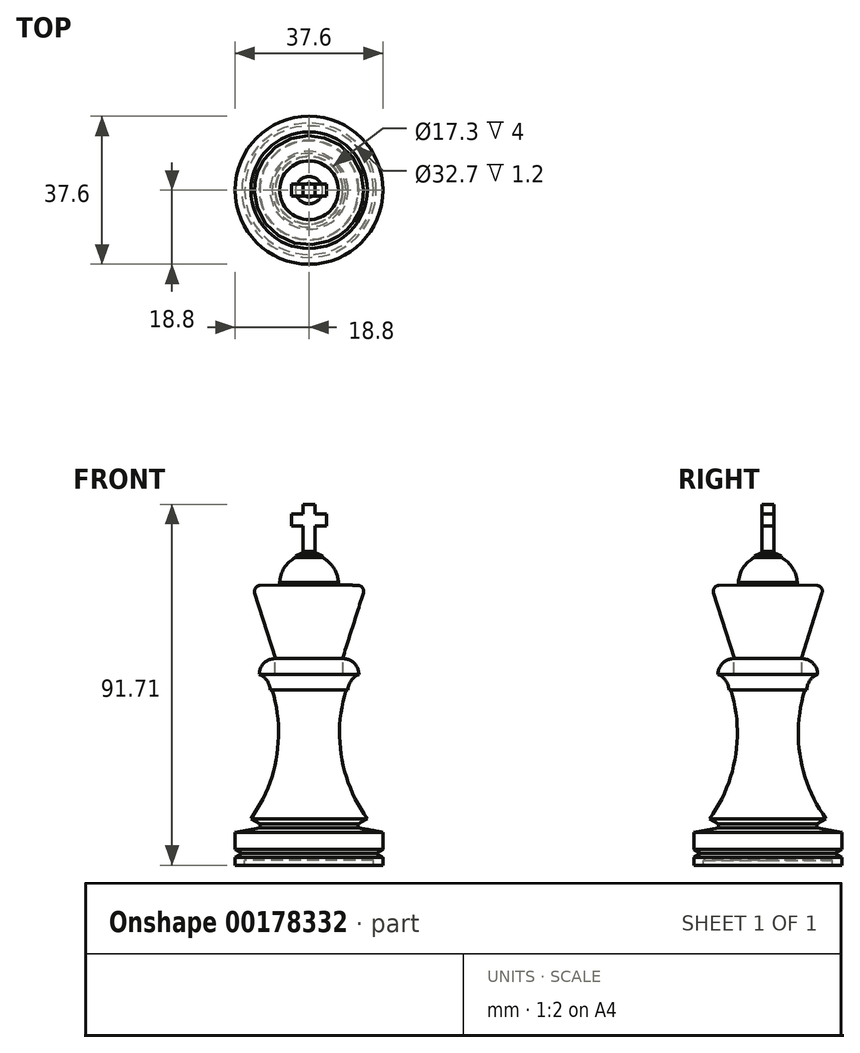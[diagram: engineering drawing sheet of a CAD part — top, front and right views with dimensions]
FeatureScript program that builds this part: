
annotation { "Feature Type Name" : "Feature", "Feature Type Description" : "" }
export const myFeature = defineFeature(function(context is Context, id is Id, definition is map)
    precondition{}
    {
        {
            var Q0;
            Q0=qCreatedBy(makeId("Front.planeOp"),FACE);
            var sketch = newSketch(context, id + "F0", { "sketchPlane" : qUnion([Q0])});
            skLineSegment(sketch, "E0", {"start": v(18.8, 2) * mm, "end": v(17.07, 3) * mm});
            skLineSegment(sketch, "E1", {"start": v(18.8, 0) * mm, "end": v(16.35, 0) * mm});
            skLineSegment(sketch, "E2", {"start": v(18.8, 0) * mm, "end": v(18.8, 2) * mm});
            skLineSegment(sketch, "E3", {"start": v(0, 79) * mm, "end": v(0, 0) * mm});
            skLineSegment(sketch, "E4", {"start": v(12.5, 9.5) * mm, "end": v(12.5, 10.5) * mm});
            skLineSegment(sketch, "E5", {"start": v(35.59, 2) * mm, "end": v(35.59, 3) * mm});
            skLineSegment(sketch, "E6", {"start": v(18.8, 4) * mm, "end": v(17.07, 3) * mm});
            skLineSegment(sketch, "E7", {"start": v(12.5, 9.5) * mm, "end": v(18.8, 8.36) * mm});
            skLineSegment(sketch, "E8", {"start": v(18.8, 4) * mm, "end": v(18.8, 8.36) * mm});
            skLineSegment(sketch, "E9", {"start": v(16.35, 1.2) * mm, "end": v(16.35, 0) * mm});
            skLineSegment(sketch, "E10", {"start": v(0, 1.2) * mm, "end": v(16.35, 1.2) * mm});
            skLineSegment(sketch, "E11", {"start": v(12.5, 10.5) * mm, "end": v(14.8, 11.83) * mm});
            skPoint(sketch, "E12.end.orphan", {"position": v(0, 13) * mm});
            skLineSegment(sketch, "E13", {"start": v(12.5, 9.5) * mm, "end": v(0, 9.5) * mm});
            skLineSegment(sketch, "E14", {"start": v(0, 9.5) * mm, "end": v(0, 44.5) * mm});
            skLineSegment(sketch, "E15", {"start": v(0, 44.5) * mm, "end": v(9.36, 44.5) * mm});
            skLineSegment(sketch, "E16", {"start": v(0, 34.34) * mm, "end": v(7.75, 34.34) * mm});
            skLineSegment(sketch, "E17", {"start": v(0, 44.5) * mm, "end": v(10.2, 44.5) * mm});
            skLineSegment(sketch, "E18", {"start": v(0, 52.5) * mm, "end": v(8.65, 52.5) * mm});
            skLineSegment(sketch, "E19", {"start": v(0, 48.5) * mm, "end": v(12.65, 48.5) * mm});
            skArc(sketch, "E20", {"start": v(12.65, 48.5) * mm, "mid": v(10.66, 46.92) * mm, "end": v(9.91, 44.5) * mm});
            skLineSegment(sketch, "E21", {"start": v(8.65, 48.5) * mm, "end": v(8.65, 52.5) * mm});
            skArc(sketch, "E22", {"start": v(12.65, 48.5) * mm, "mid": v(11.48, 51.33) * mm, "end": v(8.65, 52.5) * mm});
            skLineSegment(sketch, "E23", {"start": v(8.5, 52.5) * mm, "end": v(13.8, 69.15) * mm});
            skLineSegment(sketch, "E24", {"start": v(7.45, 71.28) * mm, "end": v(12.42, 71.1) * mm});
            skPoint(sketch, "E25.orphan", {"position": v(14.7, 72) * mm});
            skPoint(sketch, "E26.visualSharp", {"position": v(14.4, 71.04) * mm});
            skArc(sketch, "E26.filletArc", {"start": v(13.8, 69.15) * mm, "mid": v(13.6, 70.47) * mm, "end": v(12.42, 71.1) * mm});
            skLineSegment(sketch, "E27", {"start": v(0, 64.24) * mm, "end": v(7.45, 64.24) * mm});
            skLineSegment(sketch, "E28", {"start": v(7.45, 64.24) * mm, "end": v(7.45, 85.78) * mm});
            skArc(sketch, "E29", {"start": v(7.45, 71.28) * mm, "mid": v(6.44, 75.29) * mm, "end": v(3.46, 78.14) * mm});
            skLineSegment(sketch, "E30", {"start": v(3.46, 73.92) * mm, "end": v(3.46, 78.59) * mm});
            skLineSegment(sketch, "E31", {"start": v(3.46, 78.14) * mm, "end": v(0, 78.14) * mm});
            skLineSegment(sketch, "E32", {"start": v(0, 79.4) * mm, "end": v(1.73, 79.4) * mm});
            skLineSegment(sketch, "E33", {"start": v(2.15, 81.63) * mm, "end": v(2.15, 73.59) * mm});
            skLineSegment(sketch, "E34", {"start": v(1.73, 79.4) * mm, "end": v(3.46, 78.59) * mm});
            skLineSegment(sketch, "E35.trimOffspring", {"start": v(3.46, 79.4) * mm, "end": v(3.46, 90.88) * mm});
            skLineSegment(sketch, "E36", {"start": v(0, 79.4) * mm, "end": v(0, 91.4) * mm});
            skLineSegment(sketch, "E37", {"start": v(0, 79) * mm, "end": v(0, 79.4) * mm});
            skLineSegment(sketch, "E38", {"start": v(9.36, 44.5) * mm, "end": v(54.88, 44.5) * mm});
            skLineSegment(sketch, "E39", {"start": v(12.5, 10.5) * mm, "end": v(0, 10.5) * mm});
            skArc(sketch, "E40", {"start": v(9.36, 44.5) * mm, "mid": v(8.25, 27.53) * mm, "end": v(14.8, 11.83) * mm});
            skLineSegment(sketch, "E41", {"start": v(0, 79.4) * mm, "end": v(-62.4, 79.4) * mm});
            skSolve(sketch);
        }
        {
            var Q0;
            Q0=makeQuery(id+"F0.imprint","IMPRINT",FACE,{"disambiguationData":[TD([[makeQuery(id+"F0.imprint","IMPRINT",EDGE,{"derivedFrom":sQuery(id+"F0.wireOp",EDGE,"v3yrn3lP-V5wF-JRG4-7Msx-MGjZiqY3t1m5")}),1.0]])]});
            var Q1;
            Q1=makeQuery(id+"F0.imprint","IMPRINT",FACE,{"disambiguationData":[TD([[makeQuery(id+"F0.imprint","IMPRINT",EDGE,{"derivedFrom":sQuery(id+"F0.wireOp",EDGE,"v3yrn3lP-V5wF-JRG4-7Msx-MGjZiqY3t1m5")}),-1.0]])]});
            var Q2;
            Q2=makeQuery(id+"F0.imprint","IMPRINT",FACE,{"disambiguationData":[TD([[makeQuery(id+"F0.imprint","IMPRINT",EDGE,{"derivedFrom":sQuery(id+"F0.wireOp",EDGE,"xEQ1ZHFC-Zhoz-YJoE-ieFn-0IP2HIuzJ3NM")}),1.0]])]});
            var Q3;
            Q3=makeQuery(id+"F0.imprint","IMPRINT",FACE,{"disambiguationData":[TD([[makeQuery(id+"F0.imprint","IMPRINT",EDGE,{"derivedFrom":sQuery(id+"F0.wireOp",EDGE,"E0")}),1.0]])]});
            var Q4;
            Q4=makeQuery(id+"F0.imprint","IMPRINT",FACE,{"disambiguationData":[TD([[makeQuery(id+"F0.imprint","IMPRINT",EDGE,{"derivedFrom":sQuery(id+"F0.wireOp",EDGE,"nyWY0tnP-Jj6n-QFmL-lNrs-mm1IDGyNNZQy")}),-1.0]])]});
            var Q5;
            Q5=makeQuery(id+"F0.imprint","IMPRINT",FACE,{"disambiguationData":[TD([[makeQuery(id+"F0.imprint","IMPRINT",EDGE,{"derivedFrom":sQuery(id+"F0.wireOp",EDGE,"i1j5DUh5-1iJj-gxXq-cqqf-45IapP1yzGEN")}),-1.0]])]});
            var Q6;
            Q6=makeQuery(id+"F0.imprint","IMPRINT",FACE,{"disambiguationData":[TD([[makeQuery(id+"F0.imprint","IMPRINT",EDGE,{"derivedFrom":sQuery(id+"F0.wireOp",EDGE,"E4")}),1.0]])]});
            var Q7;
            {var subQ3=sQuery(id+"F0.wireOp",EDGE,"E16");Q7=makeQuery(id+"F0.imprint","IMPRINT",FACE,{"disambiguationData":[TD([[makeQuery(id+"F0.imprint","IMPRINT",EDGE,{"derivedFrom":subQ3}),1.0]])]});}
            var Q8;
            {var subQ6=sQuery(id+"F0.wireOp",EDGE,"E20");Q8=makeQuery(id+"F0.imprint","IMPRINT",FACE,{"disambiguationData":[TD([[makeQuery(id+"F0.imprint","IMPRINT",EDGE,{"derivedFrom":subQ6}),-1.0]])]});}
            var Q9;
            {var subQ2=sQuery(id+"F0.wireOp",EDGE,"E21");Q9=makeQuery(id+"F0.imprint","IMPRINT",FACE,{"disambiguationData":[TD([[makeQuery(id+"F0.imprint","IMPRINT",EDGE,{"derivedFrom":subQ2}),-1.0]])]});}
            var Q10;
            {var subQ1=sQuery(id+"F0.wireOp",EDGE,"E23");Q10=makeQuery(id+"F0.imprint","IMPRINT",FACE,{"disambiguationData":[TD([[makeQuery(id+"F0.imprint","IMPRINT",EDGE,{"derivedFrom":subQ1}),1.0]])]});}
            var Q11;
            {var subQ4=sQuery(id+"F0.wireOp",EDGE,"E27");Q11=makeQuery(id+"F0.imprint","IMPRINT",FACE,{"disambiguationData":[TD([[makeQuery(id+"F0.imprint","IMPRINT",EDGE,{"derivedFrom":subQ4}),1.0]])]});}
            var Q12;
            {var subQ0=sQuery(id+"F0.wireOp",EDGE,"E32");Q12=makeQuery(id+"F0.imprint","IMPRINT",FACE,{"disambiguationData":[TD([[makeQuery(id+"F0.imprint","IMPRINT",EDGE,{"derivedFrom":subQ0}),-1.0]])]});}
            var Q13;
            {var subQ3=sQuery(id+"F0.wireOp",EDGE,"E34");var subQ5=sQuery(id+"F0.wireOp",EDGE,"E33");var subQ7=makeQuery(id+"F0.imprint","INTERSECT",VERTEX,{"derivedFrom":[subQ5,subQ3]});Q13=makeQuery(id+"F0.imprint","IMPRINT",FACE,{"disambiguationData":[TD([[makeQuery(id+"F0.imprint","IMPRINT",EDGE,{"disambiguationData":[TD([[subQ7,-1.0]])],"derivedFrom":subQ5}),1.0]])]});}
            var Q14;
            {var subQ3=sQuery(id+"F0.wireOp",EDGE,"E11");Q14=makeQuery(id+"F0.imprint","IMPRINT",FACE,{"disambiguationData":[TD([[makeQuery(id+"F0.imprint","IMPRINT",EDGE,{"derivedFrom":subQ3}),1.0]])]});}
            var Q15;
            Q15=sQuery(id+"F0.wireOp",EDGE,"E3");
            revolve(context, id + "F1", {"surfaceOperationType" : NewSurfaceOperationType.NEW, "entities" : qUnion([Q0, Q1, Q2, Q3, Q4, Q5, Q6, Q7, Q8, Q9, Q10, Q11, Q12, Q13, Q14]), "axis" : qUnion([Q15]), "revolveType" : RevolveType.FULL});
        }
        {
            var Q0;
            Q0=qCreatedBy(makeId("Front.planeOp"),FACE);
            var sketch = newSketch(context, id + "F2", { "sketchPlane" : qUnion([Q0])});
            skLineSegment(sketch, "E42", {"start": v(0, 91.71) * mm, "end": v(1.5, 91.71) * mm});
            skLineSegment(sketch, "E43", {"start": v(1.5, 91.71) * mm, "end": v(1.5, 89.21) * mm});
            skLineSegment(sketch, "E44", {"start": v(1.5, 79.71) * mm, "end": v(0, 79.71) * mm});
            skLineSegment(sketch, "E45", {"start": v(1.5, 89.21) * mm, "end": v(4.5, 89.21) * mm});
            skLineSegment(sketch, "E46", {"start": v(4.5, 89.21) * mm, "end": v(4.5, 86.21) * mm});
            skLineSegment(sketch, "E47", {"start": v(4.5, 86.21) * mm, "end": v(1.5, 86.21) * mm});
            skLineSegment(sketch, "E48", {"start": v(0, 91.71) * mm, "end": v(-1.5, 91.71) * mm});
            skLineSegment(sketch, "E49", {"start": v(-1.5, 91.71) * mm, "end": v(-1.5, 89.21) * mm});
            skLineSegment(sketch, "E50", {"start": v(-1.5, 79.71) * mm, "end": v(0, 79.71) * mm});
            skLineSegment(sketch, "E51", {"start": v(-1.5, 89.21) * mm, "end": v(-4.5, 89.21) * mm});
            skLineSegment(sketch, "E52", {"start": v(-4.5, 89.21) * mm, "end": v(-4.5, 86.21) * mm});
            skLineSegment(sketch, "E53", {"start": v(-4.5, 86.21) * mm, "end": v(-1.5, 86.21) * mm});
            skLineSegment(sketch, "E54.trimOffspring", {"start": v(-1.5, 86.21) * mm, "end": v(-1.5, 79.71) * mm});
            skLineSegment(sketch, "E55.trimOffspring", {"start": v(1.5, 86.21) * mm, "end": v(1.5, 79.71) * mm});
            skSolve(sketch);
        }
        {
            var Q0;
            Q0 = qSketchRegion(id + "F2", true);
            extrude(context, id + "F3", {"entities" : qUnion([Q0]), "depth" : 3 * mm, "offsetDistance" : 25 * mm, "symmetric" : true});
        }
    });
